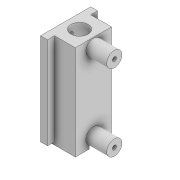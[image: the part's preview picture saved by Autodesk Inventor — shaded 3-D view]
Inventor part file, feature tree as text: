
AUTODESK INVENTOR PART (.ipt)
format: ipt  version: 2022 (Build 260153000, 153)  size: 174,080 bytes
history: native  units: mm
features: extrude x6, sketch x6, projected_geometry x1
ambient origin geometry x8: Origin, YZ Plane, XZ Plane, XY Plane, X Axis, Y Axis, Z Axis, Center Point
bodies: Solid1 (feature_tree)
feature tree (13):
  extrude  "Extrusion1"  Depth=10.0mm
  extrude  "Extrusion2"  Depth=10.0mm
  sketch  "Sketch3"  dims[d4=13.0mm d5=66.0mm d6=0.0mm]
  extrude  "Extrusion3"  Depth=66.0mm TaperAngle=0.0deg
  extrude  "Extrusion6"  Depth=5.0mm
  extrude  "Extrusion7"  Depth=13.0mm
  extrude  "Extrusion8"  Depth=2.0mm TaperAngle=0.0deg
  sketch  "Sketch1"  dims[d0=12.3mm d1=10.0mm]
  sketch  "Sketch2"  dims[d2=10.0mm d3=13.0mm]
  projected_geometry  "Projected Loop1"
  sketch  "Sketch6"  dims[d7=2.9mm d8=5.0mm]
  sketch  "Sketch7"  dims[d9=2.9mm d11=13.0mm]
  sketch  "Sketch8"  dims[d12=13.0mm d13=55.0mm d14=0.0mm d15=4.0mm d16=4.0mm d17=15.0mm d18=0.0mm d19=3.2mm d20=3.2mm d21=3.2mm d22=3.2mm d23=4.0mm d24=4.0mm d25=4.0mm d26=4.0mm d31=5.0mm d32=5.0mm d33=0.0mm d34=5.0mm d35=5.0mm d36=0.0mm d37=10.0mm d38=10.0mm d39=2.0mm d40=0.0mm d41=55.0mm]
